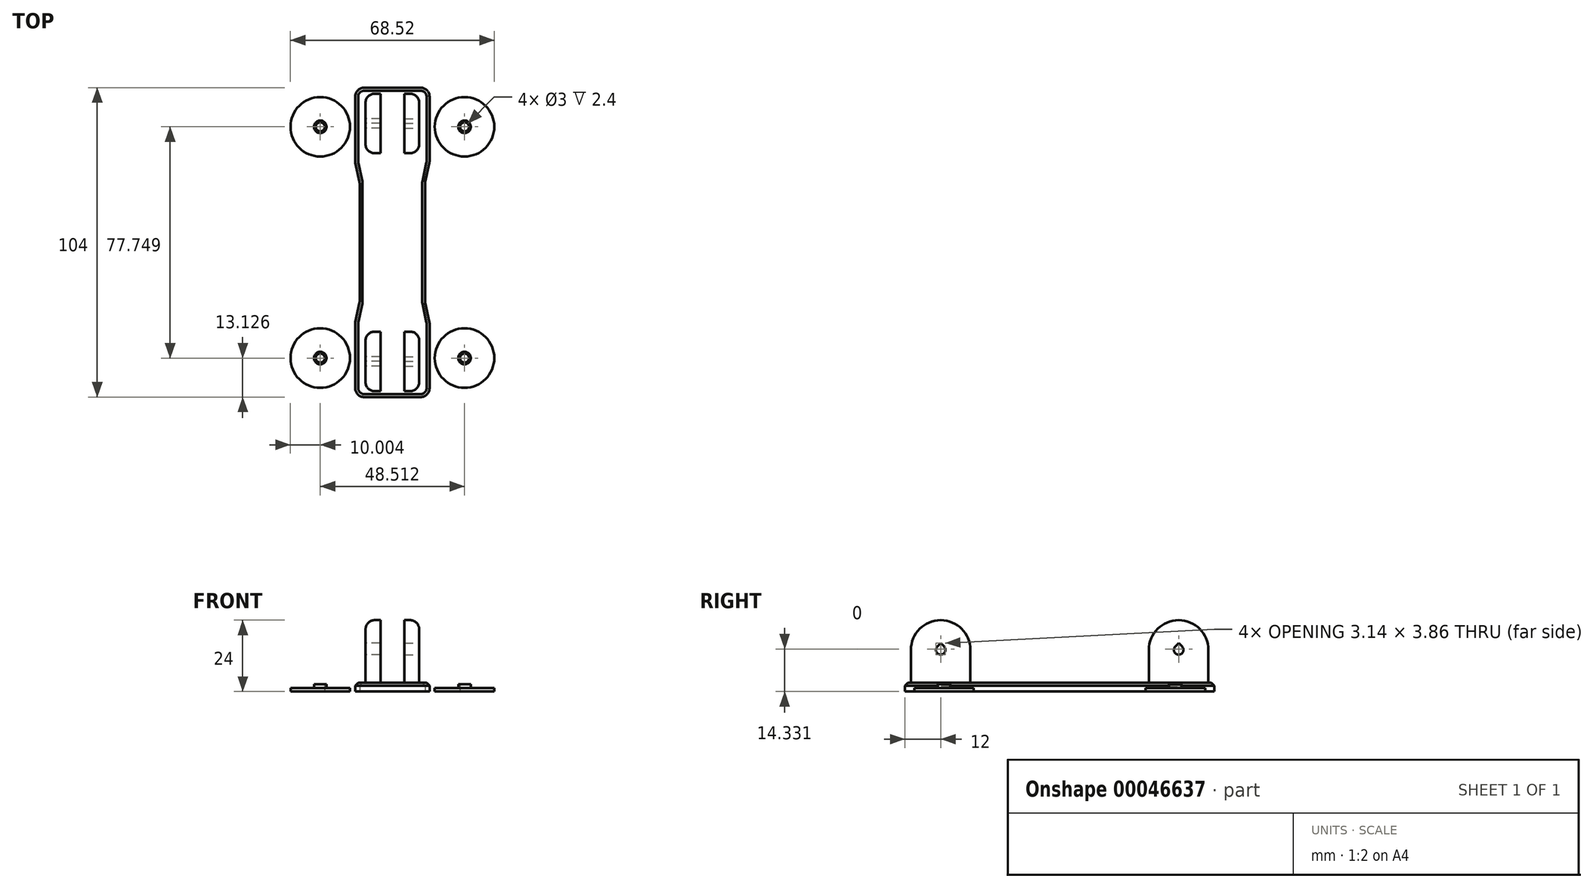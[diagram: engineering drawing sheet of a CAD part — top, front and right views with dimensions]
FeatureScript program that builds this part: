
annotation { "Feature Type Name" : "Feature", "Feature Type Description" : "" }
export const myFeature = defineFeature(function(context is Context, id is Id, definition is map)
    precondition{}
    {
        {
            var Q0;
            Q0=qCreatedBy(makeId("Top.planeOp"),FACE);
            var sketch = newSketch(context, id + "F0", { "sketchPlane" : qUnion([Q0])});
            skLineSegment(sketch, "E0.bottom", {"start": v(-4.5, -50) * mm, "end": v(4.5, -50) * mm});
            skLineSegment(sketch, "E0.top", {"start": v(-4.5, 50) * mm, "end": v(4.5, 50) * mm});
            skLineSegment(sketch, "E0.left", {"start": v(-4.5, -50) * mm, "end": v(-4.5, 50) * mm});
            skLineSegment(sketch, "E0.right", {"start": v(4.5, -50) * mm, "end": v(4.5, 50) * mm});
            skLineSegment(sketch, "E1", {"start": v(-4.5, 50) * mm, "end": v(4.5, -50) * mm, "construction": true});
            skSolve(sketch);
        }
        {
            var Q0;
            Q0=makeQuery(id+"F0.imprint","IMPRINT",FACE,{"disambiguationData":[TD([[makeQuery(id+"F0.imprint","IMPRINT",EDGE,{"derivedFrom":sQuery(id+"F0.wireOp",EDGE,"E0.bottom")}),1.0]])]});
            extrude(context, id + "F1", {"entities" : qUnion([Q0]), "depth" : 3 * mm});
        }
        {
            var Q0;
            Q0=makeQuery(id+"F1.opExtrude","SWEPT_FACE",FACE,{"disambiguationData":[OSD([sQuery(id+"F0.wireOp",EDGE,"E0.left")])]});
            var sketch = newSketch(context, id + "F2", { "sketchPlane" : qUnion([Q0])});
            skLineSegment(sketch, "E2.bottom", {"start": v(0, 3) * mm, "end": v(-40, 3) * mm, "construction": true});
            skLineSegment(sketch, "E2.top", {"start": v(0, 14) * mm, "end": v(-40, 14) * mm, "construction": true});
            skLineSegment(sketch, "E2.left", {"start": v(0, 3) * mm, "end": v(0, 14) * mm, "construction": true});
            skLineSegment(sketch, "E2.right", {"start": v(-40, 3) * mm, "end": v(-40, 14) * mm, "construction": true});
            skCircle(sketch, "E3", {"center": v(-40, 14) * mm, "radius": 1.6 * mm});
            skLineSegment(sketch, "E4", {"start": v(-40, 14) * mm, "end": v(-40, 16.26) * mm, "construction": true});
            skLineSegment(sketch, "E5", {"start": v(-40, 16.26) * mm, "end": v(-41.13, 15.13) * mm});
            skLineSegment(sketch, "E6", {"start": v(-40, 16.26) * mm, "end": v(-38.87, 15.13) * mm});
            skCircle(sketch, "E7", {"center": v(-40, 14) * mm, "radius": 10 * mm});
            skLineSegment(sketch, "E8", {"start": v(-30, 14) * mm, "end": v(-30, 3) * mm});
            skLineSegment(sketch, "E9", {"start": v(-30, 3) * mm, "end": v(-50, 3) * mm});
            skLineSegment(sketch, "E10", {"start": v(-50, 3) * mm, "end": v(-50, 14) * mm});
            skCircle(sketch, "E11", {"center": v(-40, 14) * mm, "radius": 8 * mm, "construction": true});
            skSolve(sketch);
        }
        {
            var Q0;
            {var subQ0=sQuery(id+"F2.wireOp",EDGE,"E10");Q0=makeQuery(id+"F2.imprint","IMPRINT",FACE,{"disambiguationData":[TD([[makeQuery(id+"F2.imprint","IMPRINT",EDGE,{"derivedFrom":subQ0}),-1.0]])]});}
            var Q1;
            {var subQ6=sQuery(id+"F2.wireOp",EDGE,"E5");Q1=makeQuery(id+"F2.imprint","IMPRINT",FACE,{"disambiguationData":[TD([[makeQuery(id+"F2.imprint","IMPRINT",EDGE,{"derivedFrom":subQ6}),-1.0]])]});}
            var Q2;
            {var subQ3=sQuery(id+"F2.wireOp",EDGE,"E8");Q2=makeQuery(id+"F2.imprint","IMPRINT",FACE,{"disambiguationData":[TD([[makeQuery(id+"F2.imprint","IMPRINT",EDGE,{"derivedFrom":subQ3}),-1.0]])]});}
            extrude(context, id + "F3", {"entities" : qUnion([Q0, Q1, Q2]), "oppositeDirection" : true, "depth" : 5 * mm});
        }
        {
            var Q0;
            Q0=makeQuery(id+"F3.opExtrude","SWEPT_BODY",BODY,{"disambiguationData":[OSD([sQuery(id+"F2.wireOp",EDGE,"E3"),sQuery(id+"F2.wireOp",EDGE,"E5"),sQuery(id+"F2.wireOp",EDGE,"E6"),sQuery(id+"F2.wireOp",EDGE,"E7"),sQuery(id+"F2.wireOp",EDGE,"E8"),sQuery(id+"F2.wireOp",EDGE,"E9"),sQuery(id+"F2.wireOp",EDGE,"E10")])]});
            var Q1;
            Q1=qCreatedBy(makeId("Front.planeOp"),FACE);
            mirror(context, id + "F4", {"operationType" : NewBodyOperationType.ADD, "entities" : qUnion([Q0]), "mirrorPlane" : qUnion([Q1])});
        }
        {
            var Q0;
            Q0=qCreatedBy(makeId("Top.planeOp"),FACE);
            var sketch = newSketch(context, id + "F5", { "sketchPlane" : qUnion([Q0])});
            skCircle(sketch, "E12", {"center": v(-19.76, 38.87) * mm, "radius": 1.5 * mm});
            skCircle(sketch, "E13", {"center": v(-19.76, 38.87) * mm, "radius": 10 * mm});
            skSolve(sketch);
        }
        {
            var Q0;
            Q0=makeQuery(id+"F5.imprint","IMPRINT",FACE,{"disambiguationData":[TD([[makeQuery(id+"F5.imprint","IMPRINT",EDGE,{"derivedFrom":sQuery(id+"F5.wireOp",EDGE,"E12")}),-1.0]])]});
            extrude(context, id + "F6", {"entities" : qUnion([Q0]), "depth" : 1.2 * mm});
        }
        {
            var Q0;
            Q0=makeQuery(id+"F6.opExtrude","CAP_FACE",FACE,{"disambiguationData":[OSD([sQuery(id+"F5.wireOp",EDGE,"E12"),sQuery(id+"F5.wireOp",EDGE,"E13")])],"isStart":false});
            var sketch = newSketch(context, id + "F7", { "sketchPlane" : qUnion([Q0])});
            skCircle(sketch, "E14.0", {"center": v(-19.76, 38.87) * mm, "radius": 1.5 * mm});
            skCircle(sketch, "E15", {"center": v(-19.76, 38.87) * mm, "radius": 2.1 * mm});
            skSolve(sketch);
        }
        {
            var Q0;
            Q0 = qSketchRegion(id + "F7", true);
            extrude(context, id + "F8", {"entities" : qUnion([Q0]), "operationType" : NewBodyOperationType.ADD, "depth" : 1.2 * mm});
        }
        {
            var Q0;
            Q0=makeQuery(id+"F6.opExtrude","SWEPT_BODY",BODY,{"disambiguationData":[OSD([sQuery(id+"F5.wireOp",EDGE,"E12"),sQuery(id+"F5.wireOp",EDGE,"E13")])]});
            var Q1;
            Q1=qCreatedBy(makeId("Front.planeOp"),FACE);
            mirror(context, id + "F9", {"entities" : qUnion([Q0]), "mirrorPlane" : qUnion([Q1])});
        }
        {
            var Q0;
            Q0=makeQuery(id+"F6.opExtrude","SWEPT_BODY",BODY,{"disambiguationData":[OSD([sQuery(id+"F5.wireOp",EDGE,"E12"),sQuery(id+"F5.wireOp",EDGE,"E13")])]});
            var Q1;
            Q1=makeQuery(id+"F9.opPattern","COPY",BODY,{"derivedFrom":makeQuery(id+"F6.opExtrude","SWEPT_BODY",BODY,{"disambiguationData":[OSD([sQuery(id+"F5.wireOp",EDGE,"E12"),sQuery(id+"F5.wireOp",EDGE,"E13")])]}),"instanceName":"1"});
            var Q2;
            Q2=makeQuery(id+"F1.opExtrude","SWEPT_BODY",BODY,{"disambiguationData":[OSD([sQuery(id+"F0.wireOp",EDGE,"E0.bottom"),sQuery(id+"F0.wireOp",EDGE,"E0.top"),sQuery(id+"F0.wireOp",EDGE,"E0.left"),sQuery(id+"F0.wireOp",EDGE,"E0.right")])]});
            var Q3;
            Q3=makeQuery(id+"F1.opExtrude","SWEPT_FACE",FACE,{"disambiguationData":[OSD([sQuery(id+"F0.wireOp",EDGE,"E0.right")])]});
            mirror(context, id + "F10", {"operationType" : NewBodyOperationType.ADD, "entities" : qUnion([Q0, Q1, Q2]), "mirrorPlane" : qUnion([Q3])});
        }
        {
            var Q0;
            Q0=qCreatedBy(makeId("Top.planeOp"),FACE);
            var sketch = newSketch(context, id + "F11", { "sketchPlane" : qUnion([Q0])});
            skLineSegment(sketch, "E16", {"start": v(-8, 52) * mm, "end": v(17, 52) * mm});
            skLineSegment(sketch, "E17", {"start": v(17, 52) * mm, "end": v(17, 27) * mm});
            skLineSegment(sketch, "E18", {"start": v(17, 27) * mm, "end": v(15.5, 20) * mm});
            skLineSegment(sketch, "E19", {"start": v(15.5, 20) * mm, "end": v(15.5, 0) * mm});
            skLineSegment(sketch, "E20", {"start": v(15.5, 0) * mm, "end": v(-6.5, 0) * mm});
            skLineSegment(sketch, "E21", {"start": v(-6.5, 0) * mm, "end": v(-6.5, 20) * mm});
            skLineSegment(sketch, "E22", {"start": v(-6.5, 20) * mm, "end": v(-8, 27) * mm});
            skLineSegment(sketch, "E23", {"start": v(-8, 27) * mm, "end": v(-8, 52) * mm});
            skLineSegment(sketch, "E24.0", {"start": v(0.5, 50) * mm, "end": v(8.5, 50) * mm, "construction": true});
            skLineSegment(sketch, "E25", {"start": v(4.5, 50) * mm, "end": v(4.5, 52) * mm, "construction": true});
            skLineSegment(sketch, "E26.MirrorCS", {"start": v(-6.5, 0) * mm, "end": v(-6.5, -20) * mm});
            skLineSegment(sketch, "E27.MirrorCS", {"start": v(15.5, -20) * mm, "end": v(15.5, 0) * mm});
            skLineSegment(sketch, "E28.MirrorCS", {"start": v(-6.5, -20) * mm, "end": v(-8, -27) * mm});
            skLineSegment(sketch, "E29.MirrorCS", {"start": v(17, -27) * mm, "end": v(15.5, -20) * mm});
            skLineSegment(sketch, "E30.MirrorCS", {"start": v(17, -52) * mm, "end": v(17, -27) * mm});
            skLineSegment(sketch, "E31.MirrorCS", {"start": v(-8, -27) * mm, "end": v(-8, -52) * mm});
            skLineSegment(sketch, "E32.MirrorCS", {"start": v(-8, -52) * mm, "end": v(17, -52) * mm});
            skSolve(sketch);
        }
        {
            var Q0;
            Q0=makeQuery(id+"F11.imprint","IMPRINT",FACE,{"disambiguationData":[TD([[makeQuery(id+"F11.imprint","IMPRINT",EDGE,{"derivedFrom":sQuery(id+"F11.wireOp",EDGE,"E16")}),-1.0]])]});
            var Q1;
            Q1=makeQuery(id+"F11.imprint","IMPRINT",FACE,{"disambiguationData":[TD([[makeQuery(id+"F11.imprint","IMPRINT",EDGE,{"derivedFrom":sQuery(id+"F11.wireOp",EDGE,"E20")}),1.0]])]});
            extrude(context, id + "F12", {"entities" : qUnion([Q0, Q1]), "operationType" : NewBodyOperationType.ADD, "depth" : 3 * mm});
        }
        {
            var Q0;
            Q0=makeQuery(id+"F12.opExtrude","SWEPT_EDGE",EDGE,{"disambiguationData":[OSD([sQuery(id+"F11.wireOp",EDGE,"E16"),sQuery(id+"F11.wireOp",EDGE,"E23")])]});
            var Q1;
            Q1=makeQuery(id+"F12.opExtrude","SWEPT_EDGE",EDGE,{"disambiguationData":[OSD([sQuery(id+"F11.wireOp",EDGE,"E16"),sQuery(id+"F11.wireOp",EDGE,"E17")])]});
            var Q2;
            Q2=makeQuery(id+"F12.opExtrude","SWEPT_EDGE",EDGE,{"disambiguationData":[OSD([sQuery(id+"F11.wireOp",EDGE,"E22"),sQuery(id+"F11.wireOp",EDGE,"E23")])]});
            var Q3;
            Q3=makeQuery(id+"F12.opExtrude","SWEPT_EDGE",EDGE,{"disambiguationData":[OSD([sQuery(id+"F11.wireOp",EDGE,"E21"),sQuery(id+"F11.wireOp",EDGE,"E22")])]});
            var Q4;
            Q4=makeQuery(id+"F12.opExtrude","SWEPT_EDGE",EDGE,{"disambiguationData":[OSD([sQuery(id+"F11.wireOp",EDGE,"E26.MirrorCS"),sQuery(id+"F11.wireOp",EDGE,"E28.MirrorCS")])]});
            var Q5;
            Q5=makeQuery(id+"F12.opExtrude","SWEPT_EDGE",EDGE,{"disambiguationData":[OSD([sQuery(id+"F11.wireOp",EDGE,"E28.MirrorCS"),sQuery(id+"F11.wireOp",EDGE,"E31.MirrorCS")])]});
            var Q6;
            Q6=makeQuery(id+"F12.opExtrude","SWEPT_EDGE",EDGE,{"disambiguationData":[OSD([sQuery(id+"F11.wireOp",EDGE,"E31.MirrorCS"),sQuery(id+"F11.wireOp",EDGE,"E32.MirrorCS")])]});
            var Q7;
            Q7=makeQuery(id+"F12.opExtrude","SWEPT_EDGE",EDGE,{"disambiguationData":[OSD([sQuery(id+"F11.wireOp",EDGE,"E30.MirrorCS"),sQuery(id+"F11.wireOp",EDGE,"E32.MirrorCS")])]});
            var Q8;
            Q8=makeQuery(id+"F12.opExtrude","SWEPT_EDGE",EDGE,{"disambiguationData":[OSD([sQuery(id+"F11.wireOp",EDGE,"E17"),sQuery(id+"F11.wireOp",EDGE,"E18")])]});
            var Q9;
            Q9=makeQuery(id+"F12.opExtrude","SWEPT_EDGE",EDGE,{"disambiguationData":[OSD([sQuery(id+"F11.wireOp",EDGE,"E18"),sQuery(id+"F11.wireOp",EDGE,"E19")])]});
            var Q10;
            Q10=makeQuery(id+"F12.opExtrude","SWEPT_EDGE",EDGE,{"disambiguationData":[OSD([sQuery(id+"F11.wireOp",EDGE,"E27.MirrorCS"),sQuery(id+"F11.wireOp",EDGE,"E29.MirrorCS")])]});
            var Q11;
            Q11=makeQuery(id+"F12.opExtrude","SWEPT_EDGE",EDGE,{"disambiguationData":[OSD([sQuery(id+"F11.wireOp",EDGE,"E29.MirrorCS"),sQuery(id+"F11.wireOp",EDGE,"E30.MirrorCS")])]});
            var Q12;
            Q12=makeQuery(id+"F10.opPattern","COPY",EDGE,{"derivedFrom":makeQuery(id+"F4.boolean.opBoolean","MERGE",EDGE,{"derivedFrom":[makeQuery(id+"F1.opExtrude","SWEPT_EDGE",EDGE,{"disambiguationData":[OSD([sQuery(id+"F0.wireOp",EDGE,"E0.bottom"),sQuery(id+"F0.wireOp",EDGE,"E0.left")])]}),makeQuery(id+"F4.opPattern","COPY",EDGE,{"derivedFrom":makeQuery(id+"F3.opExtrude","CAP_EDGE",EDGE,{"disambiguationData":[OSD([sQuery(id+"F2.wireOp",EDGE,"E10")])],"isStart":true}),"instanceName":"1"})]}),"instanceName":"1"});
            var Q13;
            Q13=makeQuery(id+"F4.boolean.opBoolean","MERGE",EDGE,{"derivedFrom":[makeQuery(id+"F1.opExtrude","SWEPT_EDGE",EDGE,{"disambiguationData":[OSD([sQuery(id+"F0.wireOp",EDGE,"E0.bottom"),sQuery(id+"F0.wireOp",EDGE,"E0.left")])]}),makeQuery(id+"F4.opPattern","COPY",EDGE,{"derivedFrom":makeQuery(id+"F3.opExtrude","CAP_EDGE",EDGE,{"disambiguationData":[OSD([sQuery(id+"F2.wireOp",EDGE,"E10")])],"isStart":true}),"instanceName":"1"})]});
            var Q14;
            Q14=makeQuery(id+"F3.opExtrude","CAP_EDGE",EDGE,{"disambiguationData":[OSD([sQuery(id+"F2.wireOp",EDGE,"E8")])],"isStart":true});
            var Q15;
            Q15=makeQuery(id+"F10.opPattern","COPY",EDGE,{"derivedFrom":makeQuery(id+"F3.opExtrude","CAP_EDGE",EDGE,{"disambiguationData":[OSD([sQuery(id+"F2.wireOp",EDGE,"E8")])],"isStart":true}),"instanceName":"1"});
            fillet(context, id + "F13", {"entities" : qUnion([Q0, Q1, Q2, Q3, Q4, Q5, Q6, Q7, Q8, Q9, Q10, Q11, Q12, Q13, Q14, Q15]), "radius" : 3 * mm, "tangentPropagation" : true, "allowEdgeOverflow" : false});
        }
        {
            var Q0;
            Q0=makeQuery(id+"F12.opExtrude","CAP_EDGE",EDGE,{"disambiguationData":[OSD([sQuery(id+"F11.wireOp",EDGE,"E19"),sQuery(id+"F11.wireOp",EDGE,"E27.MirrorCS")])],"isStart":false});
            chamfer(context, id + "F14", {"entities" : qUnion([Q0]), "width" : 1 * mm, "tangentPropagation" : true});
        }
    });
